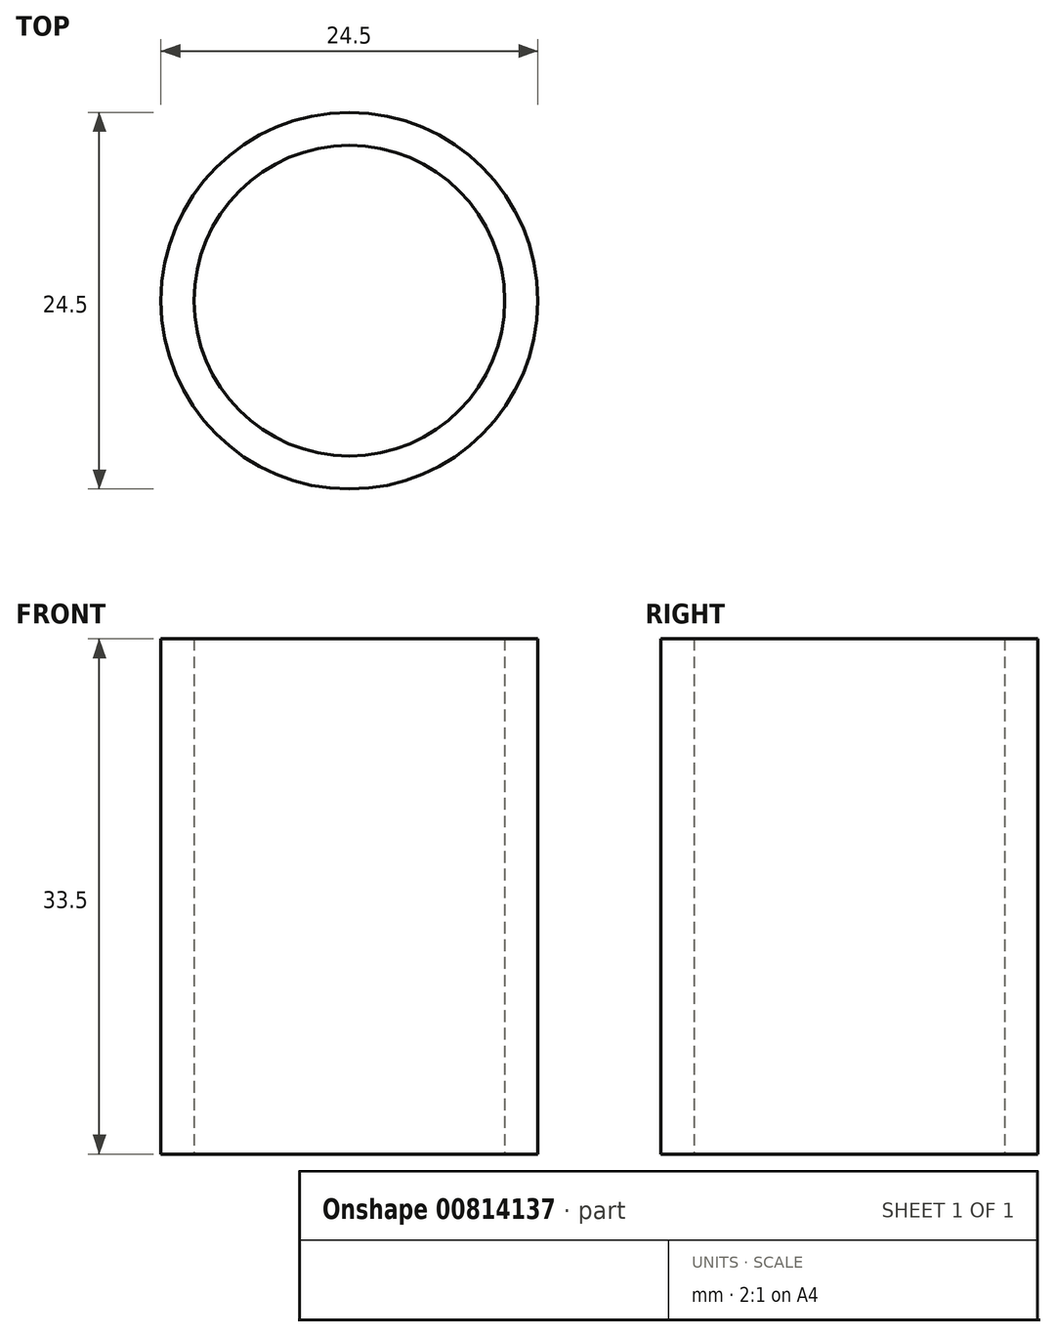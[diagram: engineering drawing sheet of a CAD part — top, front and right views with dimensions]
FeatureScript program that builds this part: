
annotation { "Feature Type Name" : "Feature", "Feature Type Description" : "" }
export const myFeature = defineFeature(function(context is Context, id is Id, definition is map)
    precondition{}
    {
        {
            var Q0;
            Q0=qCreatedBy(makeId("Top.planeOp"),FACE);
            var sketch = newSketch(context, id + "F0", { "sketchPlane" : qUnion([Q0])});
            skCircle(sketch, "E0", {"center": v(0, 0) * mm, "radius": 10.1 * mm});
            skCircle(sketch, "E1", {"center": v(0, 0) * mm, "radius": 12.25 * mm});
            skSolve(sketch);
        }
        {
            var Q0;
            Q0 = qSketchRegion(id + "F0", true);
            extrude(context, id + "F1", {"entities" : qUnion([Q0]), "depth" : 33.5 * mm, "offsetDistance" : 25 * mm});
        }
    });
